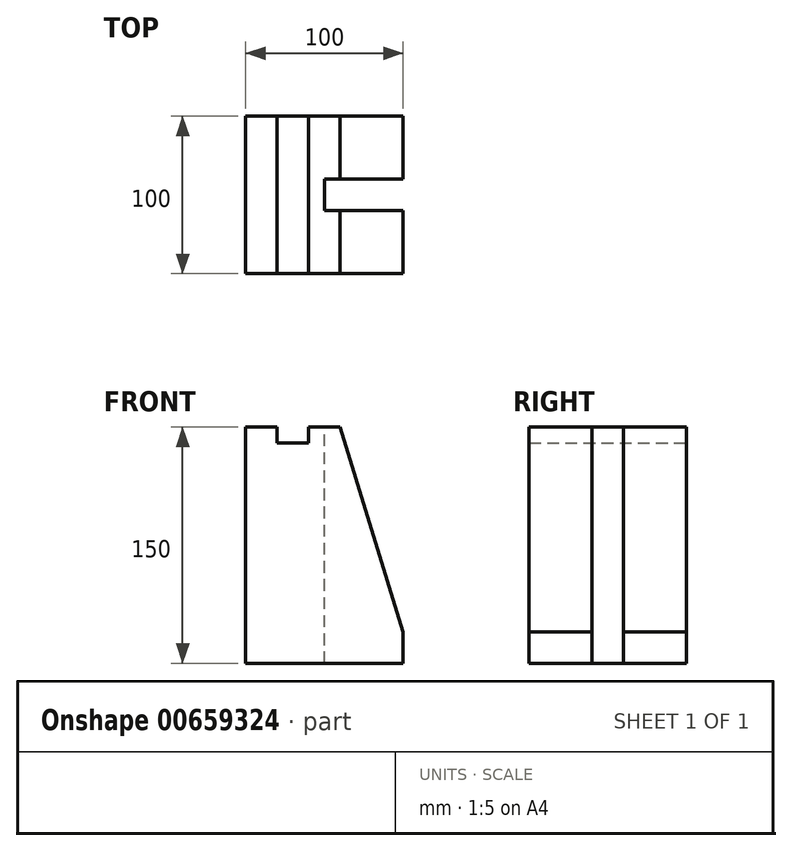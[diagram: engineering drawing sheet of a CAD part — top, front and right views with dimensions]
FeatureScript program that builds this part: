
annotation { "Feature Type Name" : "Feature", "Feature Type Description" : "" }
export const myFeature = defineFeature(function(context is Context, id is Id, definition is map)
    precondition{}
    {
        {
            var Q0;
            Q0=qCreatedBy(makeId("Front.planeOp"),FACE);
            var sketch = newSketch(context, id + "F0", { "sketchPlane" : qUnion([Q0])});
            skLineSegment(sketch, "E0.bottom", {"start": v(0, 0) * mm, "end": v(100, 0) * mm});
            skLineSegment(sketch, "E0.left", {"start": v(0, 0) * mm, "end": v(0, 150) * mm});
            skLineSegment(sketch, "E1", {"start": v(100, 0) * mm, "end": v(100, 20) * mm});
            skLineSegment(sketch, "E2", {"start": v(100, 20) * mm, "end": v(60, 150) * mm});
            skLineSegment(sketch, "E3", {"start": v(0, 150) * mm, "end": v(20, 150) * mm});
            skLineSegment(sketch, "E4", {"start": v(20, 150) * mm, "end": v(20, 140) * mm});
            skLineSegment(sketch, "E5", {"start": v(20, 140) * mm, "end": v(40, 140) * mm});
            skLineSegment(sketch, "E6", {"start": v(40, 140) * mm, "end": v(40, 150) * mm});
            skLineSegment(sketch, "E7", {"start": v(40, 150) * mm, "end": v(60, 150) * mm});
            skSolve(sketch);
        }
        {
            var Q0;
            Q0 = qSketchRegion(id + "F0", true);
            extrude(context, id + "F1", {"entities" : qUnion([Q0]), "depth" : 100 * mm, "offsetDistance" : 25 * mm});
        }
        {
            var Q0;
            Q0=makeQuery(id+"F1.opExtrude","SWEPT_FACE",FACE,{"disambiguationData":[OSD([sQuery(id+"F0.wireOp",EDGE,"E7")])]});
            var sketch = newSketch(context, id + "F2", { "sketchPlane" : qUnion([Q0])});
            skPoint(sketch, "E8.endSnap0", {"position": v(60, -50) * mm});
            skLineSegment(sketch, "E9", {"start": v(140, -50) * mm, "end": v(140, -40) * mm});
            skLineSegment(sketch, "E10", {"start": v(140, -40) * mm, "end": v(49.9, -40) * mm});
            skLineSegment(sketch, "E11", {"start": v(140, -50) * mm, "end": v(140, -60) * mm});
            skLineSegment(sketch, "E12", {"start": v(140, -60) * mm, "end": v(49.9, -60) * mm});
            skPoint(sketch, "E13.end.orphan", {"position": v(40, -50) * mm});
            skLineSegment(sketch, "E14", {"start": v(49.9, -40) * mm, "end": v(49.9, -60) * mm});
            skPoint(sketch, "E15.orphan", {"position": v(40, -60) * mm});
            skPoint(sketch, "E16.start.orphan", {"position": v(40, -40) * mm});
            skSolve(sketch);
        }
        {
            var Q0;
            Q0 = qSketchRegion(id + "F2", true);
            extrude(context, id + "F3", {"entities" : qUnion([Q0]), "operationType" : NewBodyOperationType.REMOVE, "oppositeDirection" : true, "depth" : 182 * mm, "offsetDistance" : 25 * mm});
        }
    });
